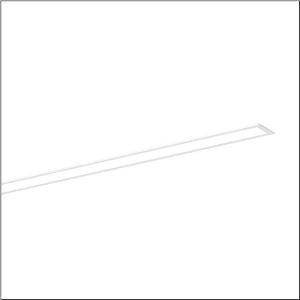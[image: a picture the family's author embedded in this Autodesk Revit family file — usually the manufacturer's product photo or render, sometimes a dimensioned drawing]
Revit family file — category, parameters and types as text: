
# Revit family: silica_r__21_51mx10db32wb_8ee9
name_source: partatom
category: Lighting Fixtures
units: mm (PartAtom-declared; Revit-internal decimal feet)

## family parameters
Cut with Voids When Loaded = No
Host = Face
Light Source = No
Part Type = Normal
Room Calculation Point = No
Round Connector Dimension = Use Diameter
Shared = No

## types (1)
- --- (1 x LED, 3000 lm, 20.2 W, 3000K)
    Apparent Load = 20 VA
    CIE Flux Codes = 48 79 96 100 100
    Color Rendering = 80
    Color Temperature = 3000K
    Default Elevation = 1800 mm
    Description = Silica® 21, office luminaire, primary optical cover: cover, of PMMA, opal, light emission: direct distribution, primary light characteristic: symmetric, installation type: recessed, LED, rated luminous flux: 3.000lm, luminous efficacy: 149lm/W, light colour: 830, colour temperature: 3000K, with terminal, 3+2-pole, max. 2.5mm², mains connection: 220..240V, AC, 50/60Hz, luminaire housing, of aluminium, traffic white (RAL 9016), length: 1.528mm, width: 79mm, height: 53mm, protection rating (complete): IP20, insulation class (complete): insulation class I (protective earthing), certification: CE, permissible operating ambient temperature: 0..+35°C, standard: EN 50419, packaging unit: 1 piece
    Height = 0 mm  [stored 0 ft]
    Lamp = 1 x LED
    Lamp Light Flux = 3000 lm
    Lamp Power = 20.2 W
    Lamp count = 1
    Length = 1527 mm
    Luminous efficacy = 149 lm/W
    Manufacturer = Siteco
    ModVariant = No
    Model = 51MX10DB32WB
    Mounting Place = Ceiling
    Mounting Type = Recessed
    Number of Poles = 1
    OnlyDefault = Yes
    Power Factor = 1
    Product Name = Silica® 21
    Product group = office luminaire | ceiling recessed
    ProductGroupID = 401
    Protection Class = Protection class I
    Protection Degree = IP 20
    RLX_Detail_Level = 1
    RLX_Emergency_Light_Flux = 0 lm
    RLX_Emergency_Type = 0
    RLX_Emergency_Type_DB = No
    RlxData = <blob elided: 20833 chars, md5=2f66b496>
    Socket = socket
    Standby Power = 0 W
    System Light Flux = 3000 lm
    System Power = 20 W
    Type Comments = factory setting: luminous flux: 100 % | dim-lin: 254 | 233 mA
    Type Image = l_1297737.jpg
    URL = http://relux.com
    VarID = @adj_047677
    Voltage = 0 V
    Weight = 0.00 kg
    Width = 79 mm

note: [stored X ft] marks values corroborated as IEEE doubles in the binary element streams (Revit-internal decimal feet)

## geometry (parser evidence)
native form markers: Blend x4, Sweep x10
no freeform markers — native parametric forms only
